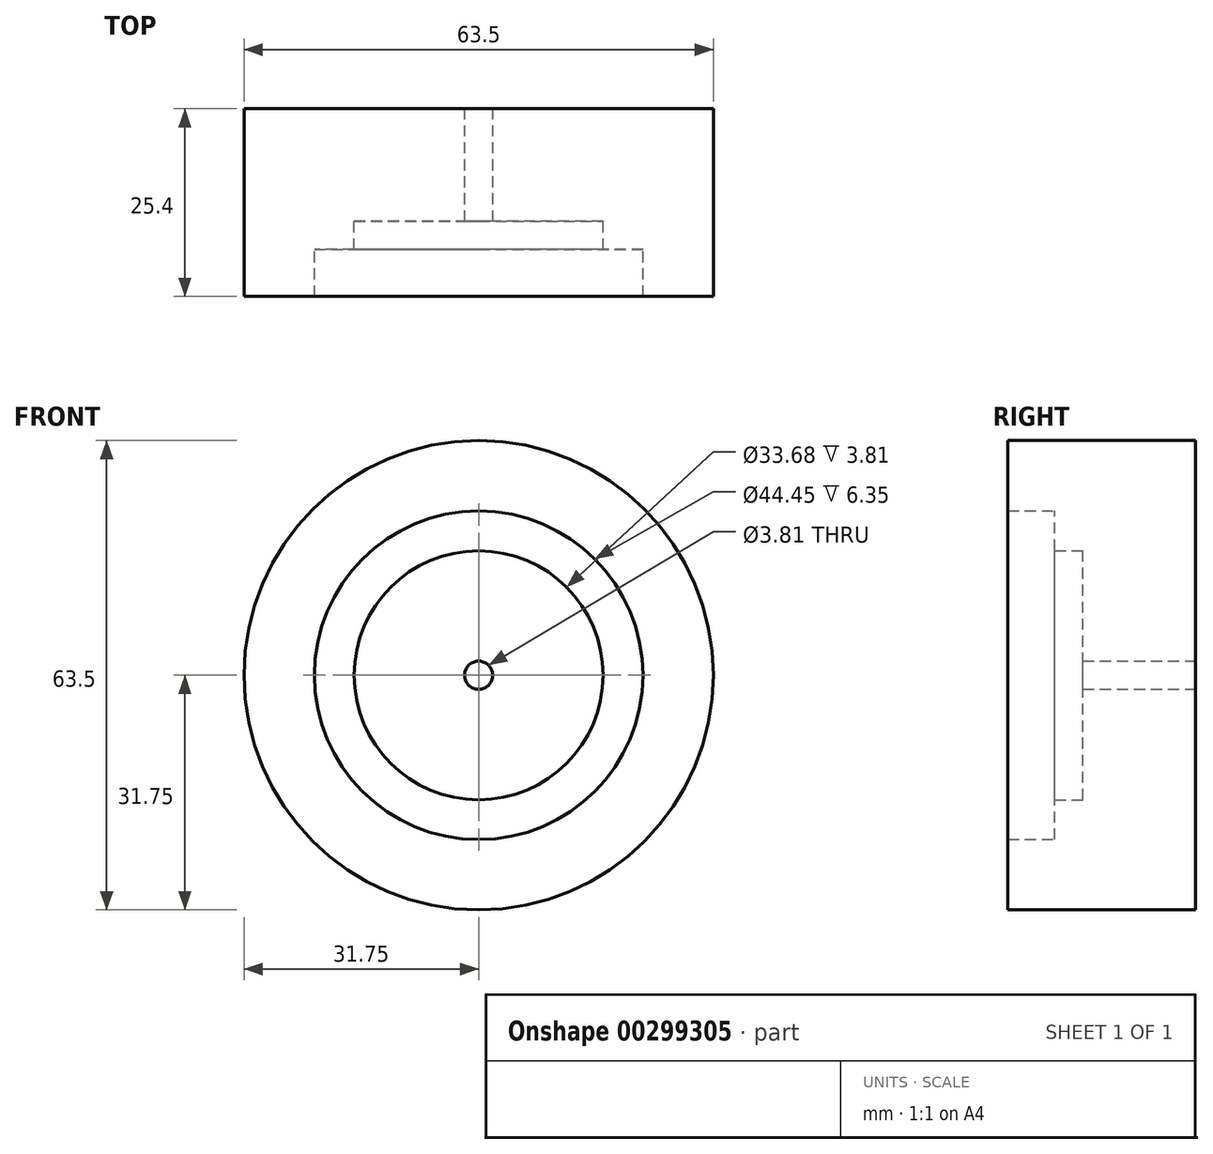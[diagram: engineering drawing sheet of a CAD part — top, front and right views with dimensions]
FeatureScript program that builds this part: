
annotation { "Feature Type Name" : "Feature", "Feature Type Description" : "" }
export const myFeature = defineFeature(function(context is Context, id is Id, definition is map)
    precondition{}
    {
        {
            var Q0;
            Q0=qCreatedBy(makeId("Front.planeOp"),FACE);
            var sketch = newSketch(context, id + "F0", { "sketchPlane" : qUnion([Q0])});
            skCircle(sketch, "E0", {"center": v(0, 0) * mm, "radius": 31.75 * mm});
            skCircle(sketch, "E1", {"center": v(0, 0) * mm, "radius": 22.23 * mm});
            skCircle(sketch, "E2", {"center": v(0, 0) * mm, "radius": 1.9 * mm});
            skCircle(sketch, "E3", {"center": v(0, 0) * mm, "radius": 16.84 * mm});
            skSolve(sketch);
        }
        {
            var Q0;
            Q0=makeQuery(id+"F0.imprint","IMPRINT",FACE,{"disambiguationData":[TD([[makeQuery(id+"F0.imprint","IMPRINT",EDGE,{"derivedFrom":sQuery(id+"F0.wireOp",EDGE,"E1")}),1.0]])]});
            extrude(context, id + "F1", {"entities" : qUnion([Q0]), "depth" : 19.05 * mm});
        }
        {
            var Q0;
            Q0=makeQuery(id+"F0.imprint","IMPRINT",FACE,{"disambiguationData":[TD([[makeQuery(id+"F0.imprint","IMPRINT",EDGE,{"derivedFrom":sQuery(id+"F0.wireOp",EDGE,"E0")}),1.0]])]});
            extrude(context, id + "F2", {"entities" : qUnion([Q0]), "operationType" : NewBodyOperationType.ADD, "depth" : 25.4 * mm});
        }
        {
            var Q0;
            Q0=sQuery(id+"F0.wireOp",EDGE,"E1");
            extrude(context, id + "F3", {"bodyType" : ToolBodyType.SURFACE, "surfaceEntities" : qUnion([Q0]), "depth" : 19.05 * mm});
        }
        {
            var Q0;
            Q0=makeQuery(id+"F0.imprint","IMPRINT",FACE,{"disambiguationData":[TD([[makeQuery(id+"F0.imprint","IMPRINT",EDGE,{"derivedFrom":sQuery(id+"F0.wireOp",EDGE,"E2")}),-1.0]])]});
            extrude(context, id + "F4", {"entities" : qUnion([Q0]), "operationType" : NewBodyOperationType.ADD, "depth" : 15.24 * mm});
        }
    });
